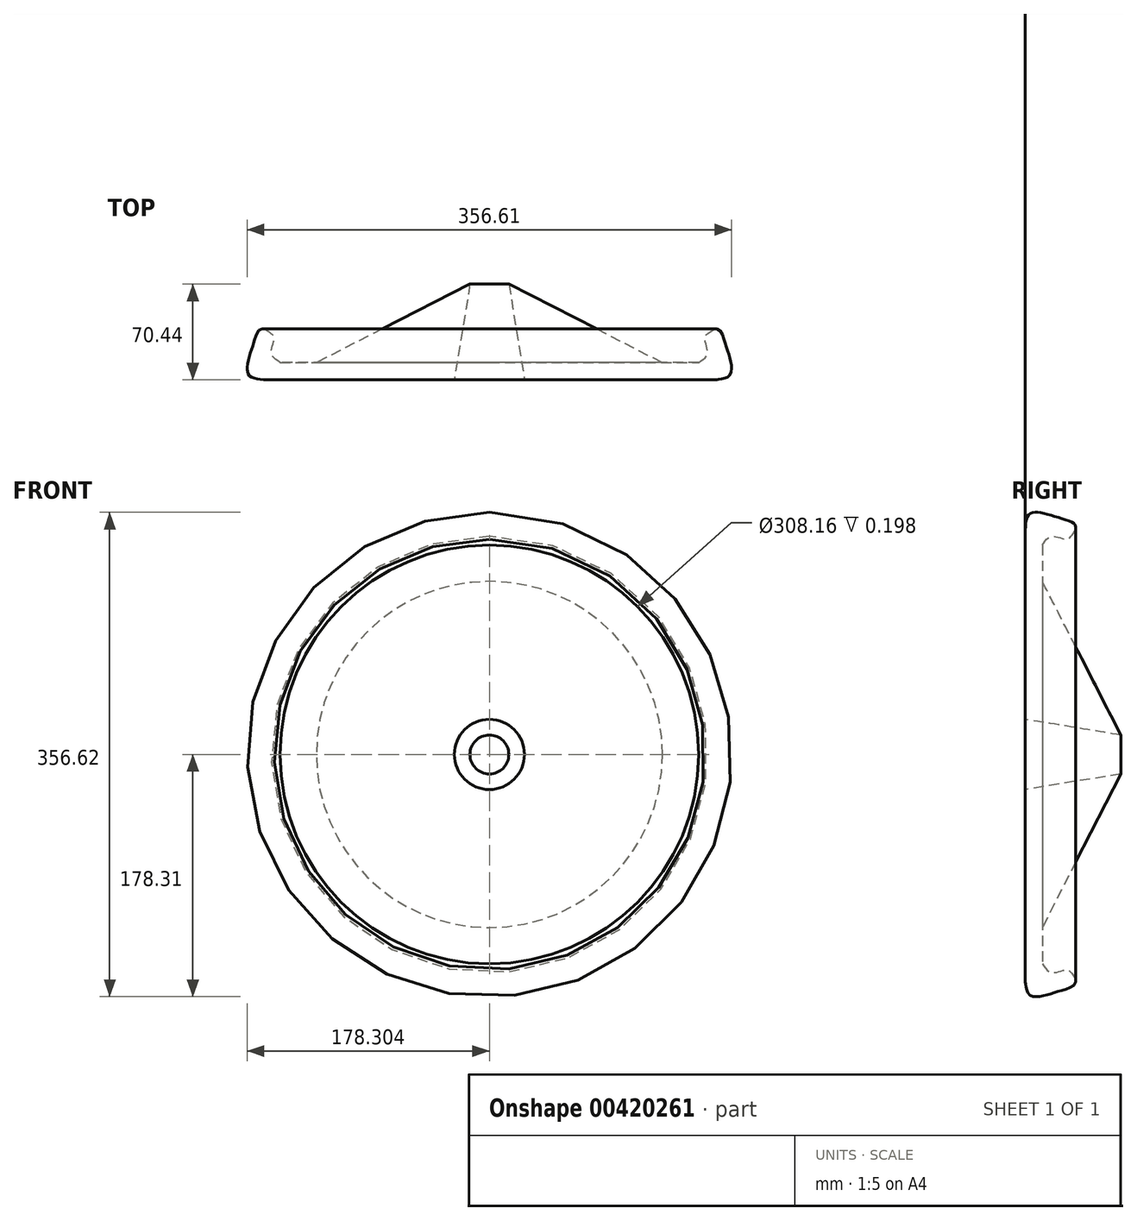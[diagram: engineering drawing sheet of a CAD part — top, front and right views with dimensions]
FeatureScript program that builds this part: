
annotation { "Feature Type Name" : "Feature", "Feature Type Description" : "" }
export const myFeature = defineFeature(function(context is Context, id is Id, definition is map)
    precondition{}
    {
        {
            var Q0;
            Q0=qCreatedBy(makeId("Top.planeOp"),FACE);
            var sketch = newSketch(context, id + "F0", { "sketchPlane" : qUnion([Q0])});
            skLineSegment(sketch, "E0", {"start": v(-31.5, 16.45) * mm, "end": v(81.58, -41.35) * mm});
            skLineSegment(sketch, "E1", {"start": v(81.58, -41.35) * mm, "end": v(108.25, -41.35) * mm});
            skLineSegment(sketch, "E2", {"start": v(108.25, -41.16) * mm, "end": v(108.25, -41.35) * mm});
            skLineSegment(sketch, "E3", {"start": v(108.25, -53.86) * mm, "end": v(-20.02, -53.86) * mm});
            skLineSegment(sketch, "E4", {"start": v(-20.02, -53.86) * mm, "end": v(-31.5, 16.45) * mm});
            skFitSpline(sketch, "E5", {"points": [v(108.25, -41.16) * mm, v(114.46, -35.3) * mm, v(113.34, -26.86) * mm, v(112.77, -22.64) * mm, v(115.02, -19.83) * mm, v(122.34, -16.73) * mm, v(127.96, -27.42) * mm, v(132.46, -45.14) * mm, v(129.65, -51.89) * mm, v(108.25, -53.86) * mm], "startDerivative": vector(77.28, 47.38) * mm, "endDerivative": vector(-156.5, 4) * mm});
            skFitSpline(sketch, "E6", {"points": [v(-7.3, -7.45) * mm, v(-11.52, -4.92) * mm, v(-10.67, 0) * mm, v(-13.48, 3.52) * mm, v(-8.7, 0) * mm, v(-7.3, -7.45) * mm]});
            skFitSpline(sketch, "E7", {"points": [v(-7.3, -12.23) * mm, v(-12.92, -11.95) * mm, v(-14.6, -7.45) * mm, v(-17.42, -7.45) * mm, v(-17.98, -14.76) * mm, v(-16.86, -20.1) * mm, v(-13.48, -23.48) * mm, v(-10.4, -24.33) * mm, v(-4.77, -23.76) * mm, v(0, -20.95) * mm, v(0, -15.05) * mm, v(-3.36, -16.45) * mm, v(-7.3, -12.23) * mm]});
            skFitSpline(sketch, "E8", {"points": [v(8.17, -22.08) * mm, v(8.17, -29.39) * mm, v(0, -37.54) * mm, v(-16.3, -31.08) * mm, v(-14.05, -40.64) * mm, v(0, -45.42) * mm, v(4.51, -49.07) * mm, v(18.3, -33.33) * mm, v(8.17, -22.08) * mm]});
            skFitSpline(sketch, "E9", {"points": [v(32.07, -26.58) * mm, v(32.36, -34.73) * mm, v(32.92, -39.23) * mm, v(26.45, -41.48) * mm, v(24.2, -45.98) * mm, v(41.92, -47.1) * mm, v(38.82, -26.3) * mm, v(32.07, -26.58) * mm]});
            skLineSegment(sketch, "E10", {"start": v(-45.83, 47.1) * mm, "end": v(-45.83, -67.08) * mm});
            skSolve(sketch);
        }
        {
            var Q0;
            Q0=makeQuery(id+"F0.imprint","IMPRINT",FACE,{"disambiguationData":[TD([[makeQuery(id+"F0.imprint","IMPRINT",EDGE,{"derivedFrom":sQuery(id+"F0.wireOp",EDGE,"E6")}),-1.0]])]});
            var Q1;
            Q1=makeQuery(id+"F0.imprint","IMPRINT",FACE,{"disambiguationData":[TD([[makeQuery(id+"F0.imprint","IMPRINT",EDGE,{"derivedFrom":sQuery(id+"F0.wireOp",EDGE,"E7")}),1.0]])]});
            var Q2;
            Q2=makeQuery(id+"F0.imprint","IMPRINT",FACE,{"disambiguationData":[TD([[makeQuery(id+"F0.imprint","IMPRINT",EDGE,{"derivedFrom":sQuery(id+"F0.wireOp",EDGE,"E8")}),1.0]])]});
            var Q3;
            Q3=makeQuery(id+"F0.imprint","IMPRINT",FACE,{"disambiguationData":[TD([[makeQuery(id+"F0.imprint","IMPRINT",EDGE,{"derivedFrom":sQuery(id+"F0.wireOp",EDGE,"E9")}),1.0]])]});
            var Q4;
            Q4=makeQuery(id+"F0.imprint","IMPRINT",FACE,{"disambiguationData":[TD([[makeQuery(id+"F0.imprint","IMPRINT",EDGE,{"derivedFrom":sQuery(id+"F0.wireOp",EDGE,"E0")}),-1.0]])]});
            var Q5;
            Q5=sQuery(id+"F0.wireOp",EDGE,"E10");
            revolve(context, id + "F1", {"entities" : qUnion([Q0, Q1, Q2, Q3, Q4]), "axis" : qUnion([Q5]), "revolveType" : RevolveType.FULL});
        }
    });
